# Revit family: Haworth_VSeries_Lateral_Attached
name_source: partatom
category: Furniture Systems
revit_build: Autodesk Revit 2018 (Build: 20170223_1515(x64)
units: mm (PartAtom-declared; Revit-internal decimal feet)

## family parameters
Always vertical = Yes
Cut with Voids When Loaded = No
OmniClass Number = 23.40.70.14.64.21
OmniClass Title = Systems Furniture
Part Type = Normal
Room Calculation Point = No
Round Connector Dimension = Use Diameter
Shared = No
Work Plane-Based = No

## types (1)
- 30w
    Actual Depth = 17"
    Actual Height = 27 1/2"
    Actual Width = 30"
    Assembly Code = E2020200
    Cabinet Finish = Haworth _ Paint _ Metallic Champagne
    Description = Haworth - VSeries - Lateral - Attached
    Drawer 1 Height = 11 15/16"
    Drawer 2 Height = 11 15/16"
    Drawer Finish = Haworth _ Paint _ Metallic Champagne
    Full Pull = No
    Manufacturer = Haworth
    Max. Width = 42"
    Min. Width = 30"
    Model = Haworth - VSeries - Lateral - Attached
    Pull Finish = Haworth _ Polymer _ Gray Tone
    Revision Number = 2
    Size = Verify Final Dim. w/ Haworth
    Stadard Height = 27.5 inches
    Standard Depth = 17 inches
    Standard Pull = Yes
    Standard Widths = 30, 36, 42 inches
    Sustainability Info = http://www.haworth.com
    Total Drawer Height = 24 1/8"
    URL = www.haworth.com
    URL - Product = http://www.haworth.com
    Warranty = http://www.haworth.com
    Width = 30"

## geometry (parser evidence)
native form markers: Sweep x7
no freeform markers — native parametric forms only
